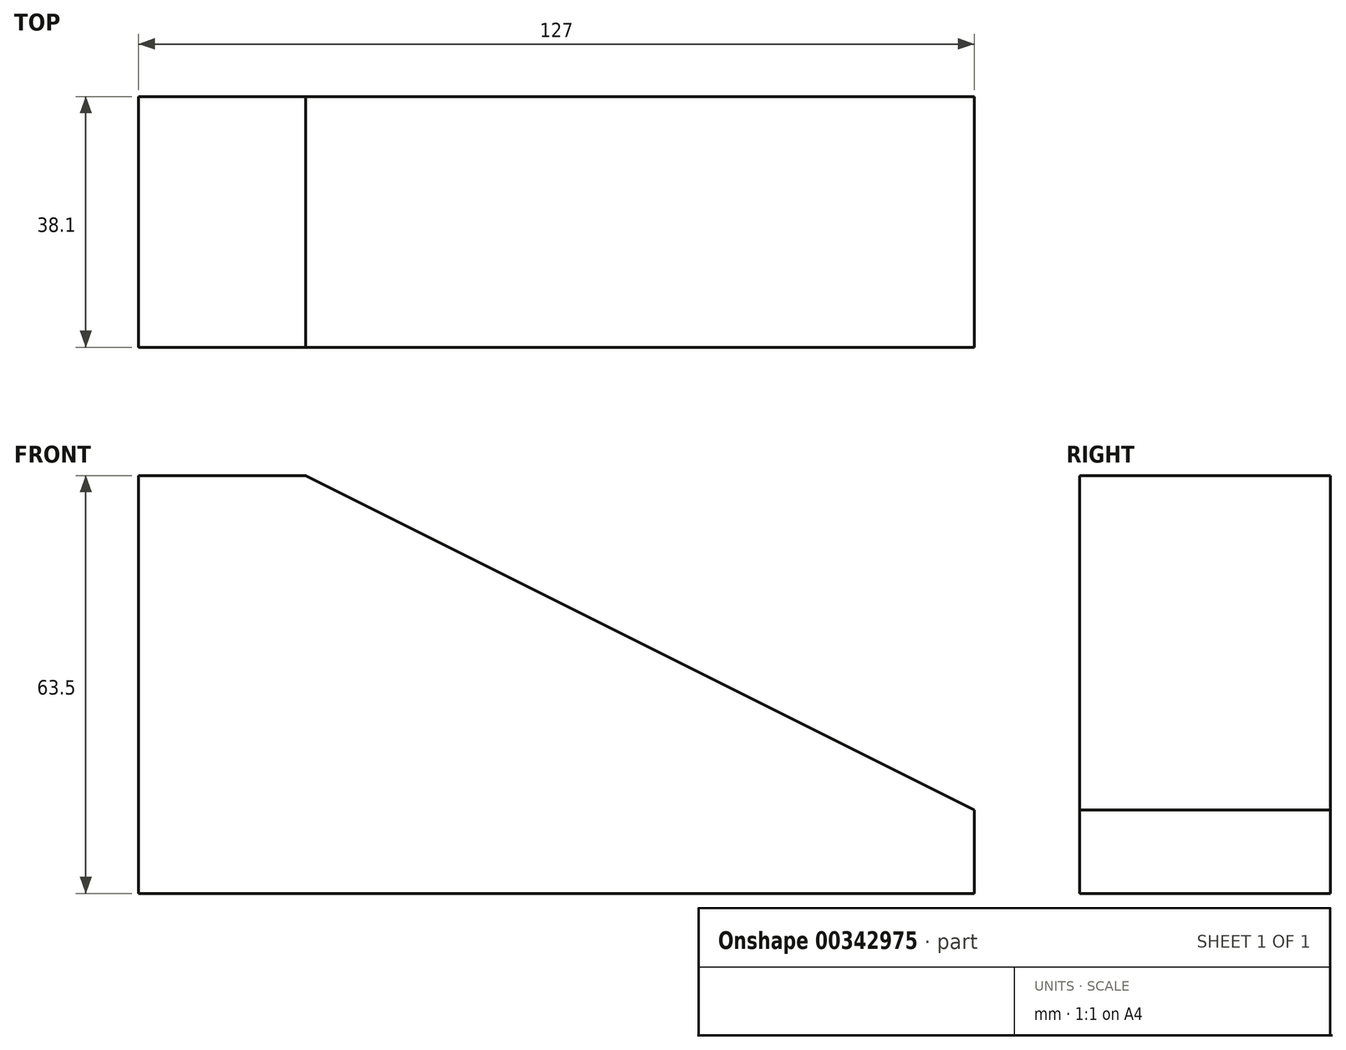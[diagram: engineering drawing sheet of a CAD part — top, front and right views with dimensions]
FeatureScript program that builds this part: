
annotation { "Feature Type Name" : "Feature", "Feature Type Description" : "" }
export const myFeature = defineFeature(function(context is Context, id is Id, definition is map)
    precondition{}
    {
        {
            var Q0;
            Q0=qCreatedBy(makeId("Front.planeOp"),FACE);
            var sketch = newSketch(context, id + "F0", { "sketchPlane" : qUnion([Q0])});
            skLineSegment(sketch, "E0", {"start": v(-68.9, -34.54) * mm, "end": v(58.1, -34.54) * mm});
            skLineSegment(sketch, "E1", {"start": v(-68.9, -34.54) * mm, "end": v(-68.9, 28.96) * mm});
            skLineSegment(sketch, "E2", {"start": v(58.1, -34.54) * mm, "end": v(58.1, -21.84) * mm});
            skLineSegment(sketch, "E3", {"start": v(-68.9, 28.96) * mm, "end": v(-43.5, 28.96) * mm});
            skLineSegment(sketch, "E4", {"start": v(58.1, -21.84) * mm, "end": v(-43.5, 28.96) * mm});
            skSolve(sketch);
        }
        {
            var Q0;
            Q0 = qSketchRegion(id + "F0", true);
            extrude(context, id + "F1", {"entities" : qUnion([Q0]), "depth" : 38.1 * mm});
        }
    });
